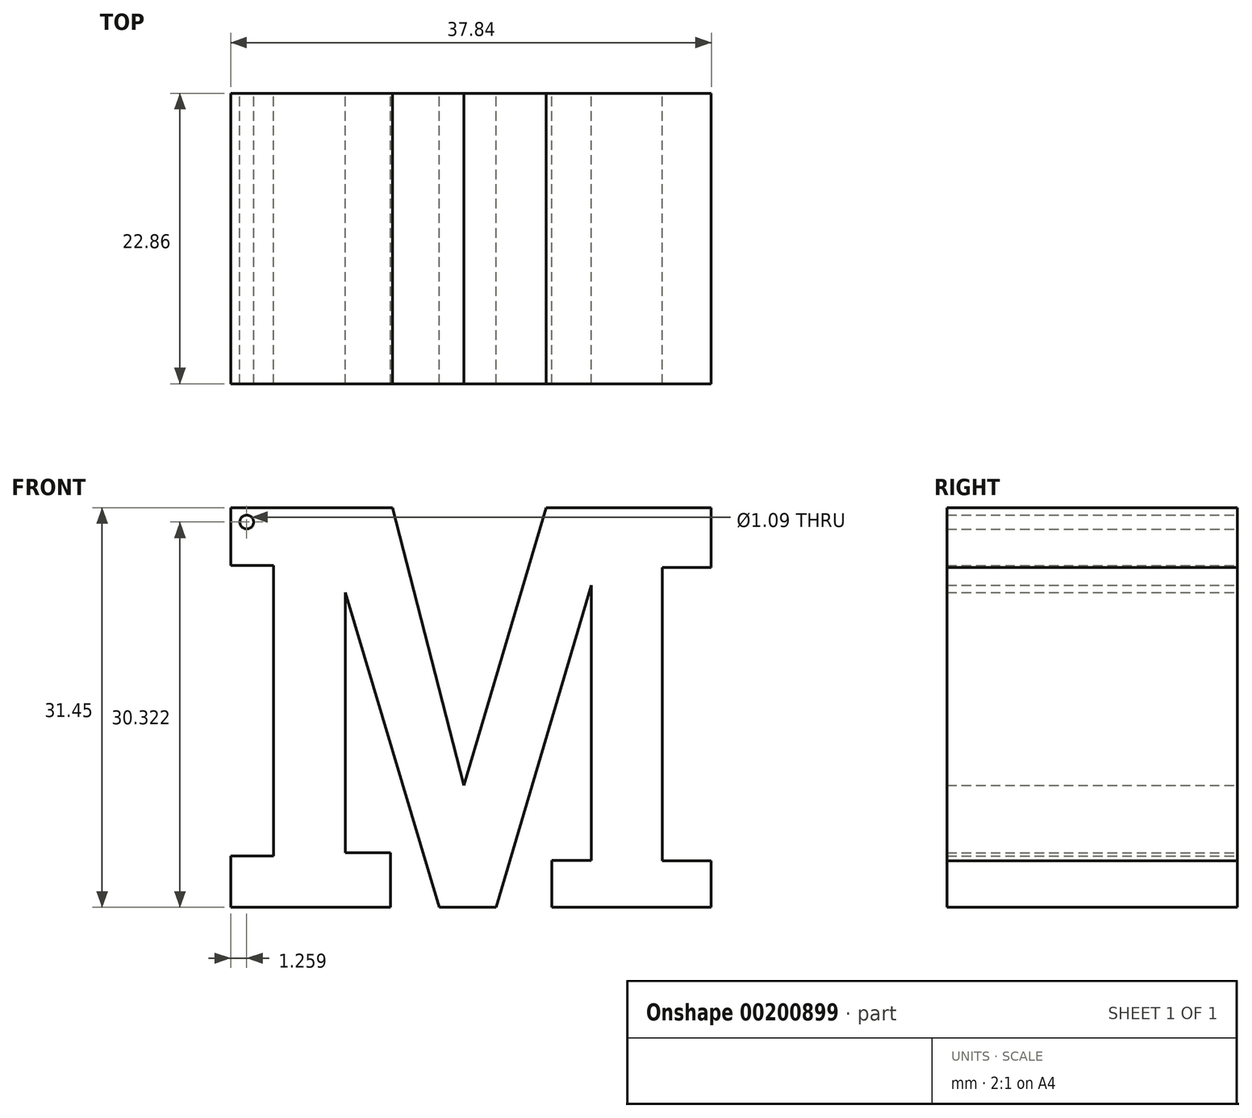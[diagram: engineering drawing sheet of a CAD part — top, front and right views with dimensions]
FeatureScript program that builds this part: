
annotation { "Feature Type Name" : "Feature", "Feature Type Description" : "" }
export const myFeature = defineFeature(function(context is Context, id is Id, definition is map)
    precondition{}
    {
        {
            var Q0;
            Q0=qCreatedBy(makeId("Front.planeOp"),FACE);
            var sketch = newSketch(context, id + "F0", { "sketchPlane" : qUnion([Q0])});
            skLineSegment(sketch, "E0", {"start": v(-57.9, 22.54) * mm, "end": v(-20.5, 22.54) * mm});
            skLineSegment(sketch, "E1", {"start": v(-57.9, 22.54) * mm, "end": v(-57.9, -14.04) * mm});
            skLineSegment(sketch, "E2", {"start": v(-19, -12.53) * mm, "end": v(-31.55, -12.53) * mm});
            skLineSegment(sketch, "E3", {"start": v(-31.55, -12.53) * mm, "end": v(-31.55, -8.84) * mm});
            skLineSegment(sketch, "E4", {"start": v(-31.55, -8.84) * mm, "end": v(-28.43, -8.84) * mm});
            skLineSegment(sketch, "E5", {"start": v(-28.43, -8.84) * mm, "end": v(-28.43, 12.81) * mm});
            skLineSegment(sketch, "E6", {"start": v(-28.43, 12.81) * mm, "end": v(-35.95, -12.53) * mm});
            skLineSegment(sketch, "E7", {"start": v(-35.95, -12.53) * mm, "end": v(-40.4, -12.53) * mm});
            skLineSegment(sketch, "E8", {"start": v(-40.4, -12.53) * mm, "end": v(-47.81, 12.24) * mm});
            skLineSegment(sketch, "E9", {"start": v(-47.81, 12.24) * mm, "end": v(-47.81, -8.24) * mm});
            skLineSegment(sketch, "E10", {"start": v(-47.81, -8.24) * mm, "end": v(-44.25, -8.24) * mm});
            skLineSegment(sketch, "E11", {"start": v(-44.25, -8.24) * mm, "end": v(-44.25, -12.53) * mm});
            skLineSegment(sketch, "E12", {"start": v(-44.25, -12.53) * mm, "end": v(-56.83, -12.53) * mm});
            skLineSegment(sketch, "E13", {"start": v(-56.83, -12.53) * mm, "end": v(-56.83, -8.48) * mm});
            skLineSegment(sketch, "E14", {"start": v(-20.58, 14.2) * mm, "end": v(-19, 14.2) * mm});
            skPoint(sketch, "E15.end.orphan", {"position": v(-17.46, -7.88) * mm});
            skLineSegment(sketch, "E16", {"start": v(-20.58, -8.87) * mm, "end": v(-19, -8.88) * mm});
            skLineSegment(sketch, "E17", {"start": v(-56.83, 18.92) * mm, "end": v(-56.83, 14.38) * mm});
            skLineSegment(sketch, "E18", {"start": v(-56.83, 14.38) * mm, "end": v(-53.47, 14.38) * mm});
            skLineSegment(sketch, "E19", {"start": v(-53.47, 14.38) * mm, "end": v(-53.47, -8.48) * mm});
            skLineSegment(sketch, "E20", {"start": v(-56.83, -8.48) * mm, "end": v(-53.47, -8.48) * mm});
            skPoint(sketch, "E21.start.orphan", {"position": v(-37.07, 0) * mm});
            skPoint(sketch, "E22.end.orphan", {"position": v(-42.75, 18.92) * mm});
            skPoint(sketch, "E23.start.orphan", {"position": v(-31.55, 18.92) * mm});
            skLineSegment(sketch, "E24", {"start": v(-38.49, -2.92) * mm, "end": v(-44.08, 18.92) * mm});
            skLineSegment(sketch, "E25", {"start": v(-38.49, -2.92) * mm, "end": v(-32, 18.92) * mm});
            skLineSegment(sketch, "E26", {"start": v(-32, 18.92) * mm, "end": v(-19, 18.92) * mm});
            skLineSegment(sketch, "E27", {"start": v(-44.08, 18.92) * mm, "end": v(-56.83, 18.92) * mm});
            skLineSegment(sketch, "E28", {"start": v(-22.87, 14.2) * mm, "end": v(-22.87, -8.87) * mm});
            skLineSegment(sketch, "E29", {"start": v(-22.87, -8.87) * mm, "end": v(-20.58, -8.87) * mm});
            skLineSegment(sketch, "E30", {"start": v(-22.87, 14.2) * mm, "end": v(-20.58, 14.2) * mm});
            skLineSegment(sketch, "E31", {"start": v(-19, 18.92) * mm, "end": v(-19, 14.2) * mm});
            skPoint(sketch, "E32.start.orphan", {"position": v(-17.46, 18.92) * mm});
            skLineSegment(sketch, "E33.trimOffspring", {"start": v(-19, -8.88) * mm, "end": v(-19, -12.53) * mm});
            skPoint(sketch, "E34.orphan", {"position": v(-17.38, -12.53) * mm});
            skCircle(sketch, "E35", {"center": v(-55.57, 17.8) * mm, "radius": 0.55 * mm});
            skSolve(sketch);
        }
        {
            var Q0;
            Q0=makeQuery(id+"F0.imprint","IMPRINT",FACE,{"disambiguationData":[TD([[makeQuery(id+"F0.imprint","IMPRINT",EDGE,{"derivedFrom":sQuery(id+"F0.wireOp",EDGE,"E2")}),-1.0]])]});
            extrude(context, id + "F1", {"entities" : qUnion([Q0]), "depth" : 22.86 * mm});
        }
    });
